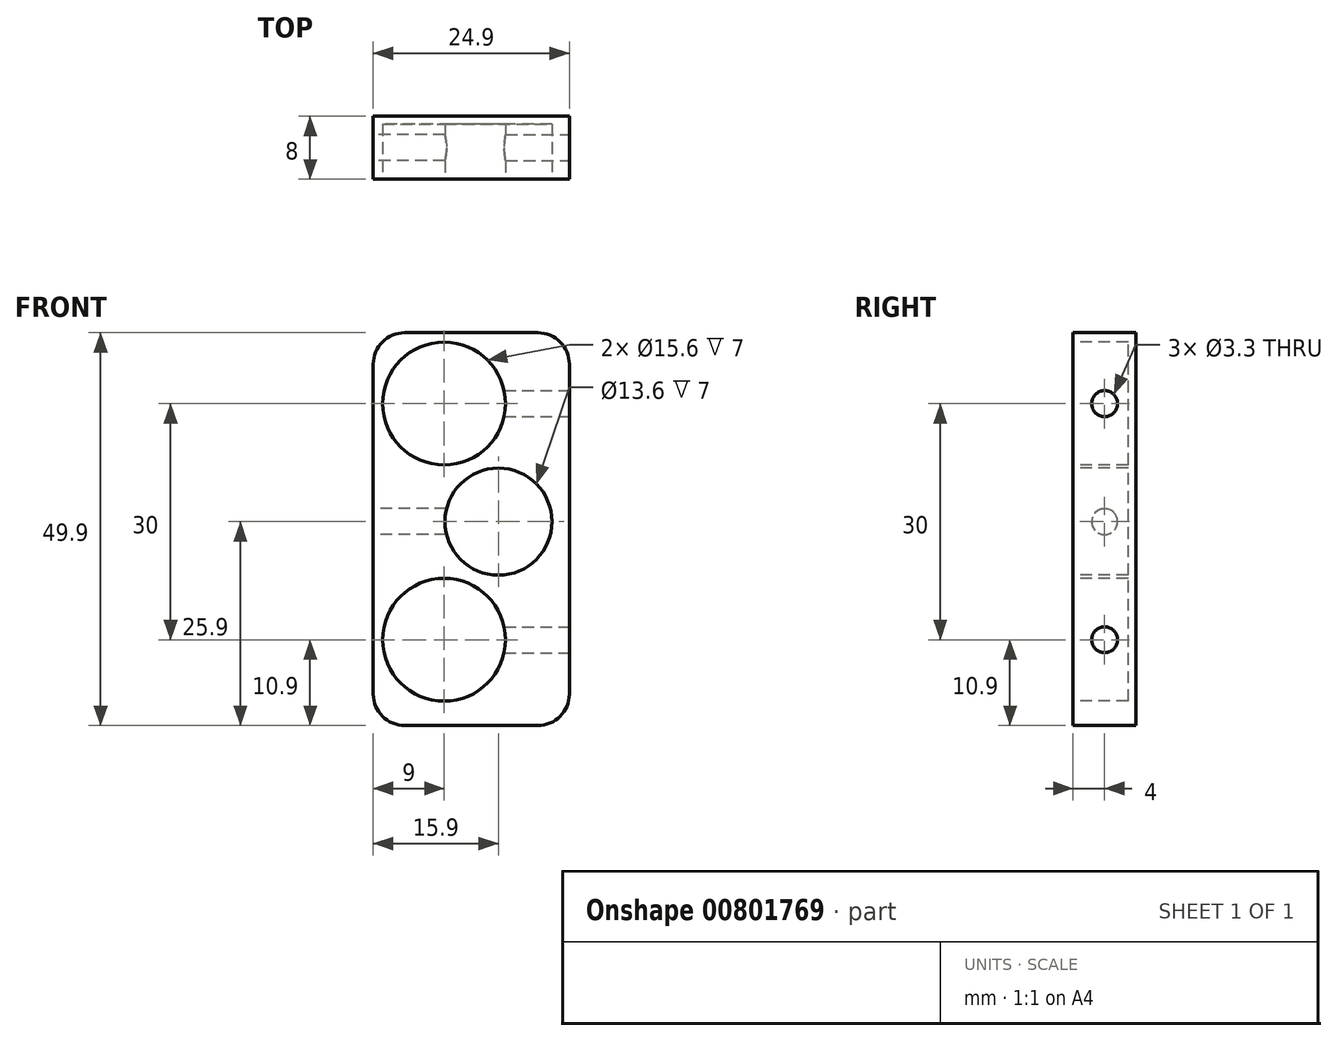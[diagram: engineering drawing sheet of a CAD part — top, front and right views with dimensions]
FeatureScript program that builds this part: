
annotation { "Feature Type Name" : "Feature", "Feature Type Description" : "" }
export const myFeature = defineFeature(function(context is Context, id is Id, definition is map)
    precondition{}
    {
        {
            var Q0;
            Q0=qCreatedBy(makeId("Front.planeOp"),FACE);
            var sketch = newSketch(context, id + "F0", { "sketchPlane" : qUnion([Q0])});
            skLineSegment(sketch, "E0.bottom", {"start": v(4, 0) * mm, "end": v(20.9, 0) * mm});
            skLineSegment(sketch, "E0.top", {"start": v(4, -49.9) * mm, "end": v(20.9, -49.9) * mm});
            skLineSegment(sketch, "E0.left", {"start": v(0, -4) * mm, "end": v(0, -45.9) * mm});
            skLineSegment(sketch, "E0.right", {"start": v(24.9, -4) * mm, "end": v(24.9, -45.9) * mm});
            skPoint(sketch, "E1.visualSharp", {"position": v(0, 0) * mm});
            skArc(sketch, "E1.filletArc", {"start": v(4, 0) * mm, "mid": v(1.17, -1.17) * mm, "end": v(0, -4) * mm});
            skPoint(sketch, "E2.visualSharp", {"position": v(24.9, 0) * mm});
            skArc(sketch, "E2.filletArc", {"start": v(24.9, -4) * mm, "mid": v(23.73, -1.17) * mm, "end": v(20.9, 0) * mm});
            skPoint(sketch, "E3.visualSharp", {"position": v(0, -49.9) * mm});
            skArc(sketch, "E3.filletArc", {"start": v(0, -45.9) * mm, "mid": v(1.17, -48.73) * mm, "end": v(4, -49.9) * mm});
            skPoint(sketch, "E4.visualSharp", {"position": v(24.9, -49.9) * mm});
            skArc(sketch, "E4.filletArc", {"start": v(20.9, -49.9) * mm, "mid": v(23.73, -48.73) * mm, "end": v(24.9, -45.9) * mm});
            skSolve(sketch);
        }
        {
            var Q0;
            Q0=qSketchRegion(id+"F0",true);
            extrude(context, id + "F1", {"entities" : qUnion([Q0]), "depth" : 8 * mm, "offsetDistance" : 25 * mm});
        }
        {
            var Q0;
            Q0=makeQuery(id+"F1.opExtrude","CAP_FACE",FACE,{"disambiguationData":[OSD([sQuery(id+"F0.wireOp",EDGE,"E0.bottom"),sQuery(id+"F0.wireOp",EDGE,"E0.top"),sQuery(id+"F0.wireOp",EDGE,"E0.left"),sQuery(id+"F0.wireOp",EDGE,"E0.right"),sQuery(id+"F0.wireOp",EDGE,"E1.filletArc"),sQuery(id+"F0.wireOp",EDGE,"E2.filletArc"),sQuery(id+"F0.wireOp",EDGE,"E3.filletArc"),sQuery(id+"F0.wireOp",EDGE,"E4.filletArc")])],"isStart":false});
            var sketch = newSketch(context, id + "F2", { "sketchPlane" : qUnion([Q0])});
            skCircle(sketch, "E5", {"center": v(9, -9) * mm, "radius": 7.8 * mm});
            skCircle(sketch, "E6", {"center": v(15.9, -24) * mm, "radius": 6.8 * mm});
            skCircle(sketch, "E7", {"center": v(9, -39) * mm, "radius": 7.8 * mm});
            skSolve(sketch);
        }
        {
            var Q0;
            Q0=qSketchRegion(id+"F2",true);
            extrude(context, id + "F3", {"entities" : qUnion([Q0]), "operationType" : NewBodyOperationType.REMOVE, "oppositeDirection" : true, "depth" : 7 * mm, "offsetDistance" : 25 * mm});
        }
        {
            var Q0;
            Q0=makeQuery(id+"F1.opExtrude","SWEPT_FACE",FACE,{"disambiguationData":[OSD([sQuery(id+"F0.wireOp",EDGE,"E0.right")])]});
            var sketch = newSketch(context, id + "F4", { "sketchPlane" : qUnion([Q0])});
            skCircle(sketch, "E8", {"center": v(-4, -9) * mm, "radius": 1.65 * mm});
            skCircle(sketch, "E9", {"center": v(-4, -39) * mm, "radius": 1.65 * mm});
            skSolve(sketch);
        }
        {
            var Q0;
            Q0=makeQuery(id+"F4.imprint","IMPRINT",FACE,{"disambiguationData":[TD([[makeQuery(id+"F4.imprint","IMPRINT",EDGE,{"derivedFrom":sQuery(id+"F4.wireOp",EDGE,"E9")}),1.0]])]});
            var Q1;
            Q1=makeQuery(id+"F4.imprint","IMPRINT",FACE,{"disambiguationData":[TD([[makeQuery(id+"F4.imprint","IMPRINT",EDGE,{"derivedFrom":sQuery(id+"F4.wireOp",EDGE,"E8")}),1.0]])]});
            extrude(context, id + "F5", {"entities" : qUnion([Q0, Q1]), "operationType" : NewBodyOperationType.REMOVE, "endBound" : BoundingType.UP_TO_NEXT, "oppositeDirection" : true, "depth" : 25 * mm, "offsetDistance" : 25 * mm});
        }
        {
            var Q0;
            Q0=makeQuery(id+"F1.opExtrude","SWEPT_FACE",FACE,{"disambiguationData":[OSD([sQuery(id+"F0.wireOp",EDGE,"E0.left")])]});
            var sketch = newSketch(context, id + "F6", { "sketchPlane" : qUnion([Q0])});
            skCircle(sketch, "E10", {"center": v(4, -24) * mm, "radius": 1.65 * mm});
            skSolve(sketch);
        }
        {
            var Q0;
            Q0=makeQuery(id+"F6.imprint","IMPRINT",FACE,{"disambiguationData":[TD([[makeQuery(id+"F6.imprint","IMPRINT",EDGE,{"derivedFrom":sQuery(id+"F6.wireOp",EDGE,"E10")}),1.0]])]});
            extrude(context, id + "F7", {"entities" : qUnion([Q0]), "operationType" : NewBodyOperationType.REMOVE, "endBound" : BoundingType.UP_TO_NEXT, "oppositeDirection" : true, "depth" : 25 * mm, "offsetDistance" : 25 * mm});
        }
    });
